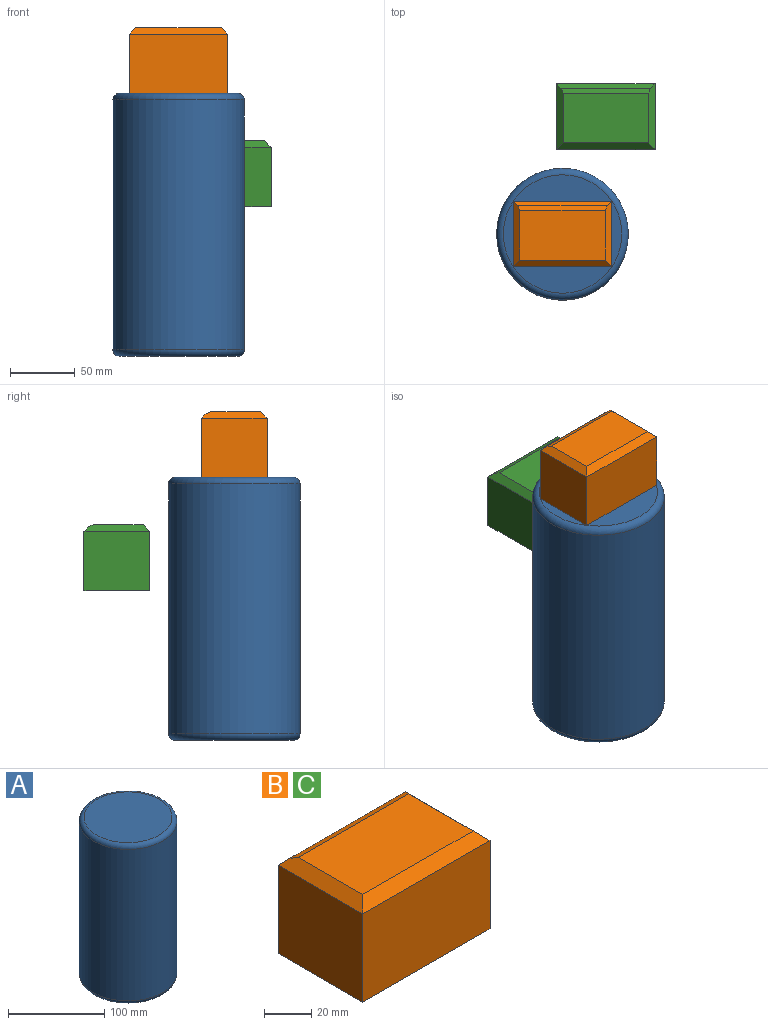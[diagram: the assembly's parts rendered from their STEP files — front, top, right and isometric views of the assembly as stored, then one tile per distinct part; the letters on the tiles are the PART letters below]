
ASSEMBLY  parts=3 mates=1
PART A: 5 faces, bbox 110x110x203.2 mm
  f0: cylinder r=50.8mm len=193.04mm, axis (0,0,-1), area 61615.6mm2, adj f3,f4
  f1: plane 91.44x91.44mm, normal (0,0,1), area 6566.9mm2, adj f4
  f2: plane 91.44x91.44mm, normal (0,0,-1), area 6566.9mm2, adj f3
  f3: torus R=45.72mm, axis (0,0,1), area 2454.4mm2, adj f0,f2
  f4: torus R=45.72mm, axis (0,0,1), area 2454.4mm2, adj f0,f1
PART B: 11 faces, bbox 76.2x50.8x50.8 mm
  f0: plane 50.8x45.72mm, normal (-1,0,0), area 2322.6mm2, adj f1,f3,f5,f7
  f1: plane 76.2x45.72mm, normal (0,-1,0), area 3483.9mm2, adj f0,f2,f5,f9
  f2: plane 50.8x45.72mm, normal (1,0,0), area 2322.6mm2, adj f1,f3,f5,f10
  f3: plane 76.2x45.72mm, normal (0,1,0), area 3483.9mm2, adj f0,f2,f5,f6
  f4: plane 66.04x38.54mm, normal (0,0,1), area 2544.9mm2, adj f7,f8,f9,f10
  f5: plane 76.2x50.8mm, normal (0,0,-1), area 3871mm2, adj f0,f1,f2,f3
  f6: plane 76.2x3.59mm, normal (0,0.71,0.71), area 368.8mm2, adj f3,f7,f8,f10
  f7: plane 50.8x5.08mm, normal (-0.71,0,0.71), area 326.2mm2, adj f0,f4,f6,f8,f9
  f8: plane 69.02x3.59mm, normal (0,0.38,0.92), area 262.6mm2, adj f4,f6,f7,f10
  f9: plane 76.2x5.08mm, normal (0,-0.71,0.71), area 510.9mm2, adj f1,f4,f7,f10
  f10: plane 50.8x5.08mm, normal (0.71,0,0.71), area 326.2mm2, adj f2,f4,f6,f8,f9
PART C: same geometry as B
PLACE A t=(-143.62,-78.19,-94.5)mm
PLACE B t=(-162.82,-83.48,108.7)mm
PLACE C t=(-129.36,7.24,21.29)mm
MATE planar B.f5 <-> A.f0  axis (0,0,-1) through (-143.62,-78.19,108.7)mm
